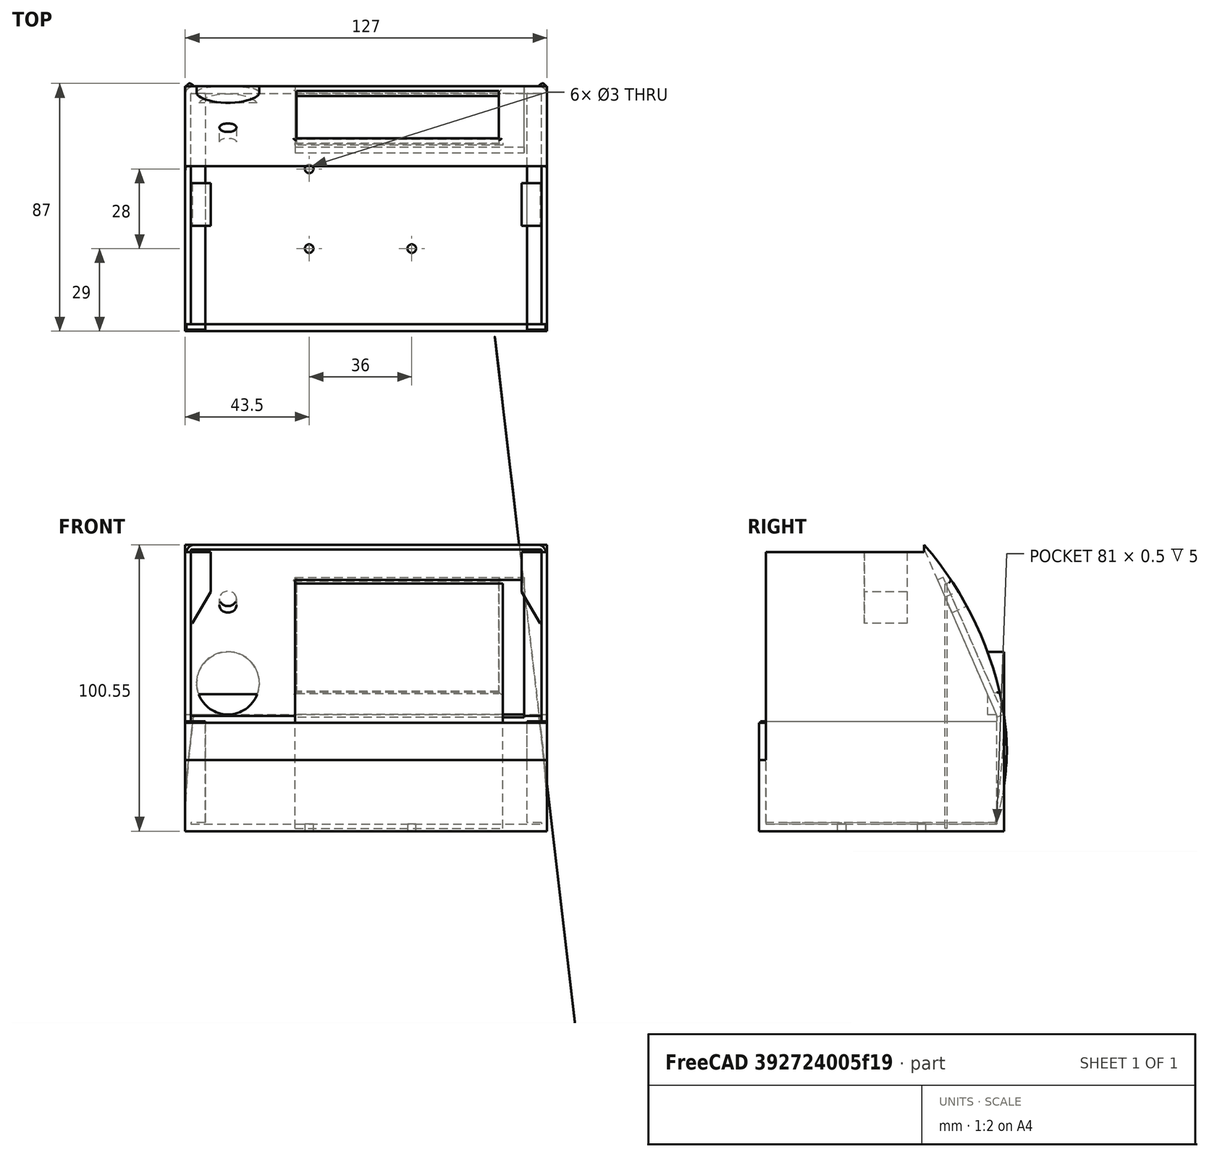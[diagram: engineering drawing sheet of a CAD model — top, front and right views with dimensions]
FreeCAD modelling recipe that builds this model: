
FCSTD DOCUMENT  (FreeCAD 0.15R4671 (Git))
Label: soldering_station
License: All rights reserved
LicenseURL: http://en.wikipedia.org/wiki/All_rights_reserved
objects: Sketcher::SketchObject×9, PartDesign::Pad×9, Part::MultiFuse×4, Part::Cut×3, Part::Chamfer×2
note: 36 computed .brp shape members not serialized (recipe doc carries the construction recipe); baked Part::Feature solids carry a one-line shape summary decoded from their .brp

FEATURE [Sketcher::SketchObject] Sketch001
  Placement = pos=(0,0,0) rot=(0.57735,0.57735,0.57735;2.0944rad)
  sketch-geometry (8):
    g0: LineSegment StartX=0 StartY=0 StartZ=0 EndX=86 EndY=0 EndZ=0
    g1: LineSegment StartX=86 StartY=0 StartZ=0 EndX=86 EndY=41 EndZ=0
    g2: ArcOfCircle CenterX=-32.4329 CenterY=21.67 CenterZ=0 NormalX=0 NormalY=0 NormalZ=1 Radius=120 StartAngle=0.161788 EndAngle=0.717263
    g3: LineSegment StartX=58 StartY=100.549 StartZ=0 EndX=58 EndY=98 EndZ=0
    g4: LineSegment StartX=0 StartY=0 StartZ=0 EndX=0 EndY=25 EndZ=0
    g5: LineSegment StartX=0 StartY=25 StartZ=0 EndX=2.5 EndY=25 EndZ=0
    g6: LineSegment StartX=2.5 StartY=25 StartZ=0 EndX=2.5 EndY=98 EndZ=0
    g7: LineSegment StartX=2.5 StartY=98 StartZ=0 EndX=58 EndY=98 EndZ=0
  constraints (24):
    c: Coincident(g0,g-1)
    c: Horizontal(g0)
    c: Coincident(g1,g0)
    c: Vertical(g1)
    c: Coincident(g2,g1)
    c: DistanceX(g0) = 86
    c: Coincident(g3,g2)
    c: Vertical(g3)
    c: Radius(g2) = 120
    c: DistanceY(g1) = 41
    c: DistanceY(g1,g2) = -19.33
    c: Coincident(g4,g-1)
    c: Vertical(g4)
    c: Coincident(g5,g4)
    c: Horizontal(g5)
    c: Coincident(g6,g5)
    c: Vertical(g6)
    c: DistanceY(g4) = 25
    c: DistanceX(g5) = 2.5
    c: Coincident(g7,g6)
    c: Coincident(g7,g3)
    c: Horizontal(g7)
    c: DistanceY(g-1,g6) = 98
    c: DistanceX(g2,g4) = -58
FEATURE [PartDesign::Pad] Pad001  label="outside"
  Length = 127
  Length2 = 100
  Midplane = true
  Placement = pos=(0,0,0) rot=(0.57735,0.57735,0.57735;2.0944rad)
  Sketch = -> Sketch001
  Type = 0
FEATURE [Sketcher::SketchObject] Sketch002
  Placement = pos=(0,0,0) rot=(0.57735,0.57735,0.57735;2.0944rad)
  sketch-geometry (8):
    g0: LineSegment StartX=56 StartY=103.5 StartZ=0 EndX=56 EndY=120 EndZ=0
    g1: LineSegment StartX=56 StartY=120 StartZ=0 EndX=0 EndY=120 EndZ=0
    g2: LineSegment StartX=56 StartY=103.5 StartZ=0 EndX=83.5 EndY=40.5 EndZ=0
    g3: LineSegment StartX=83.5 StartY=40.5 StartZ=0 EndX=83.5 EndY=2.5 EndZ=0
    g4: LineSegment StartX=0 StartY=25 StartZ=0 EndX=2.5 EndY=25 EndZ=0
    g5: LineSegment StartX=2.5 StartY=25 StartZ=0 EndX=2.5 EndY=2.5 EndZ=0
    g6: LineSegment StartX=2.5 StartY=2.5 StartZ=0 EndX=83.5 EndY=2.5 EndZ=0
    g7: LineSegment StartX=0 StartY=120 StartZ=0 EndX=0 EndY=25 EndZ=0
  constraints (24):
    c: Vertical(g0)
    c: Coincident(g1,g0)
    c: PointOnObject(g1,g-2)
    c: Horizontal(g1)
    c: DistanceY(g0,g2) = -63
    c: Coincident(g2,g0)
    c: DistanceX(g1) = -56
    c: Coincident(g3,g2)
    c: Vertical(g3)
    c: DistanceY(g3) = -38
    c: Horizontal(g4)
    c: Coincident(g5,g4)
    c: Vertical(g5)
    c: Coincident(g6,g5)
    c: Horizontal(g6)
    c: Coincident(g7,g1)
    c: Coincident(g7,g4)
    c: Vertical(g7)
    c: DistanceX(g4) = 2.5
    c: DistanceY(g-1,g5) = 2.5
    c: DistanceY(g-1,g4) = 25
    c: DistanceX(g6) = 81
    c: DistanceY(g6,g3) = 0
    c: DistanceX(g3,g6) = 0
FEATURE [PartDesign::Pad] Pad  label="inner"
  Length = 123
  Length2 = 100
  Midplane = true
  Placement = pos=(0,0,0) rot=(0.57735,0.57735,0.57735;2.0944rad)
  Sketch = -> Sketch002
  Type = 0
FEATURE [Sketcher::SketchObject] Sketch004
  Placement = pos=(0,0,3) rot=(0,0,1;0rad)
  sketch-geometry (8):
    g0: LineSegment StartX=-63 StartY=84.5 StartZ=0 EndX=-56.5 EndY=84.5 EndZ=0
    g1: LineSegment StartX=-56.5 StartY=84.5 StartZ=0 EndX=-56.5 EndY=2.5 EndZ=0
    g2: LineSegment StartX=-56.5 StartY=2.5 StartZ=0 EndX=-63 EndY=2.5 EndZ=0
    g3: LineSegment StartX=-63 StartY=2.5 StartZ=0 EndX=-63 EndY=84.5 EndZ=0
    g4: LineSegment StartX=56.5 StartY=84.5 StartZ=0 EndX=63 EndY=84.5 EndZ=0
    g5: LineSegment StartX=63 StartY=84.5 StartZ=0 EndX=63 EndY=2.5 EndZ=0
    g6: LineSegment StartX=63 StartY=2.5 StartZ=0 EndX=56.5 EndY=2.5 EndZ=0
    g7: LineSegment StartX=56.5 StartY=2.5 StartZ=0 EndX=56.5 EndY=84.5 EndZ=0
  constraints (23):
    c: Coincident(g0,g1)
    c: Coincident(g1,g2)
    c: Coincident(g2,g3)
    c: Coincident(g3,g0)
    c: Horizontal(g0)
    c: Horizontal(g2)
    c: Vertical(g1)
    c: Vertical(g3)
    c: Coincident(g4,g5)
    c: Coincident(g5,g6)
    c: Coincident(g6,g7)
    c: Coincident(g7,g4)
    c: Horizontal(g4)
    c: Horizontal(g6)
    c: Vertical(g5)
    c: Vertical(g7)
    c: DistanceY(g-1,g2) = 2.5
    c: DistanceY(g-1,g6) = 2.5
    c: DistanceY(g3) = 82
    c: DistanceY(g5) = -82
    c: DistanceX(g2,g5) = 126
    c: DistanceX(g-1,g1) = -56.5
    c: DistanceX(g1,g6) = 113
FEATURE [Sketcher::SketchObject] Sketch005
  Placement = pos=(0,84.3002,37.041) rot=(1,0,0;1.9848rad)
  sketch-geometry (5):
    g0: LineSegment StartX=-24.5 StartY=53 StartZ=0 EndX=46.5 EndY=53 EndZ=0
    g1: LineSegment StartX=46.5 StartY=53 StartZ=0 EndX=46.5 EndY=11 EndZ=0
    g2: LineSegment StartX=46.5 StartY=11 StartZ=0 EndX=-24.5 EndY=11 EndZ=0
    g3: LineSegment StartX=-24.5 StartY=11 StartZ=0 EndX=-24.5 EndY=53 EndZ=0
    g4: Circle CenterX=-48.5 CenterY=46 CenterZ=0 NormalX=0 NormalY=0 NormalZ=1 Radius=3
  constraints (15):
    c: Coincident(g0,g1)
    c: Coincident(g1,g2)
    c: Coincident(g2,g3)
    c: Coincident(g3,g0)
    c: Horizontal(g0)
    c: Horizontal(g2)
    c: Vertical(g1)
    c: Vertical(g3)
    c: DistanceX(g-1,g0) = 46.5
    c: DistanceX(g0,g0) = -71
    c: Radius(g4) = 3
    c: DistanceY(g4,g0) = 7
    c: DistanceY(g1) = -42
    c: DistanceY(g-1,g2) = 11
    c: DistanceX(g4,g0) = 24
FEATURE [PartDesign::Pad] Pad005  label="display"
  Length = 20
  Length2 = 100
  Midplane = true
  Placement = pos=(0,84.3002,37.041) rot=(1,0,0;1.9848rad)
  Reversed = true
  Sketch = -> Sketch005
  Type = 0
FEATURE [Sketcher::SketchObject] Sketch  label="holes"
  sketch-geometry (3):
    g0: Circle CenterX=-20 CenterY=29 CenterZ=0 NormalX=0 NormalY=0 NormalZ=1 Radius=1.5
    g1: Circle CenterX=16 CenterY=29 CenterZ=0 NormalX=0 NormalY=0 NormalZ=1 Radius=1.5
    g2: Circle CenterX=-20 CenterY=57 CenterZ=0 NormalX=0 NormalY=0 NormalZ=1 Radius=1.5
  constraints (9):
    c: Radius(g0) = 1.5
    c: Equal(g0,g2)
    c: Equal(g0,g1)
    c: DistanceX(g0,g1) = 36
    c: DistanceX(g-1,g0) = -20
    c: DistanceX(g1,g2) = -36
    c: DistanceY(g1,g0) = 0
    c: DistanceY(g2,g1) = -28
    c: DistanceY(g-1,g1) = 29
FEATURE [PartDesign::Pad] Pad006  label="hole extrude"
  Length = 20
  Length2 = 100
  Midplane = true
  Sketch = -> Sketch
  Type = 0
FEATURE [Sketcher::SketchObject] Sketch006  label="temporary support "
  Placement = pos=(0,0,1) rot=(0,0,1;0rad)
  sketch-geometry (4):
    g0: LineSegment StartX=-25 StartY=66.1 StartZ=0 EndX=48 EndY=66.1 EndZ=0
    g1: LineSegment StartX=48 StartY=66.1 StartZ=0 EndX=48 EndY=65.3 EndZ=0
    g2: LineSegment StartX=48 StartY=65.3 StartZ=0 EndX=-25 EndY=65.3 EndZ=0
    g3: LineSegment StartX=-25 StartY=65.3 StartZ=0 EndX=-25 EndY=66.1 EndZ=0
  constraints (12):
    c: Coincident(g0,g1)
    c: Coincident(g1,g2)
    c: Coincident(g2,g3)
    c: Coincident(g3,g0)
    c: Horizontal(g0)
    c: Horizontal(g2)
    c: Vertical(g1)
    c: Vertical(g3)
    c: DistanceY(g-1,g0) = 66.1
    c: DistanceY(g0,g2) = -0.8
    c: DistanceX(g-1,g0) = -25
    c: DistanceX(g0) = 73
FEATURE [PartDesign::Pad] Pad007  label="renfort display"
  Length = 86
  Length2 = 100
  Placement = pos=(0,0,1) rot=(0,0,1;0rad)
  Sketch = -> Sketch006
  Type = 0
FEATURE [Sketcher::SketchObject] Sketch007  label="fixation cover"
  Placement = pos=(0,0,98) rot=(0,0,1;0rad)
  sketch-geometry (8):
    g0: LineSegment StartX=-62.5 StartY=52 StartZ=0 EndX=-54.5 EndY=52 EndZ=0
    g1: LineSegment StartX=-54.5 StartY=52 StartZ=0 EndX=-54.5 EndY=37 EndZ=0
    g2: LineSegment StartX=-54.5 StartY=37 StartZ=0 EndX=-62.5 EndY=37 EndZ=0
    g3: LineSegment StartX=-62.5 StartY=37 StartZ=0 EndX=-62.5 EndY=52 EndZ=0
    g4: LineSegment StartX=62.5 StartY=52 StartZ=0 EndX=54.5 EndY=52 EndZ=0
    g5: LineSegment StartX=54.5 StartY=52 StartZ=0 EndX=54.5 EndY=37 EndZ=0
    g6: LineSegment StartX=54.5 StartY=37 StartZ=0 EndX=62.5 EndY=37 EndZ=0
    g7: LineSegment StartX=62.5 StartY=37 StartZ=0 EndX=62.5 EndY=52 EndZ=0
  constraints (24):
    c: Coincident(g0,g1)
    c: Coincident(g1,g2)
    c: Coincident(g2,g3)
    c: Coincident(g3,g0)
    c: Horizontal(g0)
    c: Horizontal(g2)
    c: Vertical(g1)
    c: Vertical(g3)
    c: Coincident(g4,g5)
    c: Coincident(g5,g6)
    c: Coincident(g6,g7)
    c: Coincident(g7,g4)
    c: Horizontal(g4)
    c: Horizontal(g6)
    c: Vertical(g5)
    c: Vertical(g7)
    c: Equal(g6,g2)
    c: Equal(g5,g1)
    c: DistanceY(g4,g0) = 0
    c: DistanceY(g1) = -15
    c: Symmetric(g0,g4,g-2)
    c: DistanceX(g2) = -8
    c: DistanceX(g6,g2) = -125
    c: DistanceY(g-1,g1) = 37
FEATURE [Sketcher::SketchObject] Sketch008  label="display inside"
  Placement = pos=(0,84.3002,37.041) rot=(1,0,0;1.9848rad)
  sketch-geometry (4):
    g0: LineSegment StartX=-25 StartY=55.5 StartZ=0 EndX=55.5 EndY=55.5 EndZ=0
    g1: LineSegment StartX=55.5 StartY=55.5 StartZ=0 EndX=55.5 EndY=3 EndZ=0
    g2: LineSegment StartX=55.5 StartY=3 StartZ=0 EndX=-25 EndY=3 EndZ=0
    g3: LineSegment StartX=-25 StartY=3 StartZ=0 EndX=-25 EndY=55.5 EndZ=0
  constraints (12):
    c: Coincident(g0,g1)
    c: Coincident(g1,g2)
    c: Coincident(g2,g3)
    c: Coincident(g3,g0)
    c: Horizontal(g0)
    c: Horizontal(g2)
    c: Vertical(g1)
    c: Vertical(g3)
    c: DistanceY(g1) = -52.5
    c: DistanceY(g-1,g1) = 3
    c: DistanceX(g0) = 80.5
    c: DistanceX(g-1,g0) = 55.5
FEATURE [PartDesign::Pad] Pad009  label="inside display"
  Length = 6
  Length2 = 100
  Midplane = true
  Placement = pos=(0,84.3002,37.041) rot=(1,0,0;1.9848rad)
  Reversed = true
  Sketch = -> Sketch008
  Type = 0
FEATURE [Sketcher::SketchObject] Sketch009  label="support jack"
  Placement = pos=(0,86,0) rot=(0,0.707107,0.707107;3.14159rad)
  sketch-geometry (1):
    g0: Circle CenterX=48.5 CenterY=52 CenterZ=0 NormalX=0 NormalY=0 NormalZ=1 Radius=11
  constraints (3):
    c: Radius(g0) = 11
    c: DistanceX(g-1,g0) = 48.5
    c: DistanceY(g-1,g0) = 52
FEATURE [PartDesign::Pad] Pad010  label="support jack001"
  Length = 5.8
  Length2 = 100
  Placement = pos=(0,86,0) rot=(0,0.707107,0.707107;3.14159rad)
  Reversed = true
  Sketch = -> Sketch009
  Type = 0
FEATURE [Part::Cut] Cut
  Base = -> Pad001
  Tool = -> Pad
FEATURE [Part::MultiFuse] Fusion
  Shapes = -> [Pad005,Pad009]
FEATURE [Part::MultiFuse] Fusion001
  Shapes = -> [Cut,Pad010]
FEATURE [Part::Cut] Cut001  label="body"
  Base = -> Fusion001
  Tool = -> Fusion
FEATURE [PartDesign::Pad] Pad011  label="support electronic"
  Length = 35.5
  Length2 = 100
  Placement = pos=(0,0,3) rot=(0,0,1;0rad)
  Sketch = -> Sketch004
  Type = 0
FEATURE [Part::MultiFuse] Fusion002
  Shapes = -> [Cut001,Pad011]
FEATURE [Part::Cut] Cut002
  Base = -> Fusion002
  Tool = -> Pad006
FEATURE [PartDesign::Pad] Pad012
  Length = 25
  Length2 = 100
  Placement = pos=(0,0,98) rot=(0,0,1;0rad)
  Reversed = true
  Sketch = -> Sketch007
  Type = 0
FEATURE [Part::Chamfer] Chamfer001
  Base = -> Pad012
  Edges = 1 edges: [Edge19 r1=11 r2=6.5]
FEATURE [Part::Chamfer] Chamfer
  Base = -> Chamfer001
  Edges = 1 edges: [Edge22 r1=11 r2=6.5]
FEATURE [Part::MultiFuse] Fusion003  label="support_cover"
  Shapes = -> [Chamfer]
